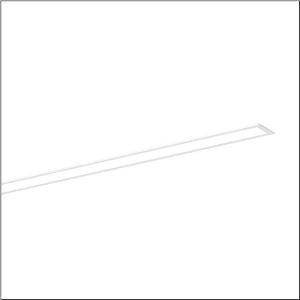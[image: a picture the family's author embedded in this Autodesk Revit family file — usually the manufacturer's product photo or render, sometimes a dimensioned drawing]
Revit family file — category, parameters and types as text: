
# Revit family: silica_r__21_51mx10dc35wb_43eb
name_source: partatom
category: Lighting Fixtures
units: mm (PartAtom-declared; Revit-internal decimal feet)

## family parameters
Cut with Voids When Loaded = No
Host = Face
Light Source = No
Part Type = Normal
Room Calculation Point = No
Round Connector Dimension = Use Diameter
Shared = No

## types (1)
- --- (1 x LED, 6000 lm, 42.6 W, 3000K)
    Apparent Load = 43 VA
    CIE Flux Codes = 48 79 96 100 100
    Color Rendering = 80
    Color Temperature = 3000K
    Default Elevation = 1800 mm
    Description = Silica® 21, office luminaire, primary optical cover: cover, of PMMA, opal, light emission: direct distribution, primary light characteristic: symmetric, installation type: recessed, LED, rated luminous flux: 6.000lm, luminous efficacy: 141lm/W, light colour: 830, colour temperature: 3000K, with terminal, 3+2-pole, max. 2.5mm², mains connection: 220..240V, AC, 50/60Hz, rated input power: 42.6W, luminaire housing, of aluminium, traffic white (RAL 9016), length: 3.028mm, width: 79mm, height: 53mm, protection rating (complete): IP20, insulation class (complete): insulation class I (protective earthing), certification: CE, permissible operating ambient temperature: 0..+35°C, standard: EN 50419, packaging unit: 1 piece
    Height = 0 mm  [stored 0 ft]
    Lamp = 1 x LED
    Lamp Light Flux = 6000 lm
    Lamp Power = 42.6 W
    Lamp count = 1
    Length = 3027 mm
    Luminous efficacy = 141 lm/W
    Manufacturer = Siteco
    ModVariant = No
    Model = 51MX10DC35WB
    Mounting Place = Ceiling
    Mounting Type = Recessed
    Number of Poles = 1
    OnlyDefault = Yes
    Power Factor = 1
    Product Name = Silica® 21
    Product group = office luminaire | ceiling recessed
    ProductGroupID = 401
    Protection Class = Protection class I
    Protection Degree = IP 20
    RLX_Detail_Level = 1
    RLX_Emergency_Light_Flux = 0 lm
    RLX_Emergency_Type = 0
    RLX_Emergency_Type_DB = No
    RlxData = <blob elided: 21249 chars, md5=71f17e81>
    Socket = socket
    Standby Power = 0 W
    System Light Flux = 6000 lm
    System Power = 43 W
    Type Comments = factory setting: luminous flux: 100 % | dim-lin: 254 | 233 mA
    Type Image = l_1297737.jpg
    URL = http://relux.com
    VarID = @adj_047635
    Voltage = 0 V
    Weight = 0.00 kg
    Width = 79 mm

note: [stored X ft] marks values corroborated as IEEE doubles in the binary element streams (Revit-internal decimal feet)

## geometry (parser evidence)
native form markers: Blend x4, Sweep x10
no freeform markers — native parametric forms only
